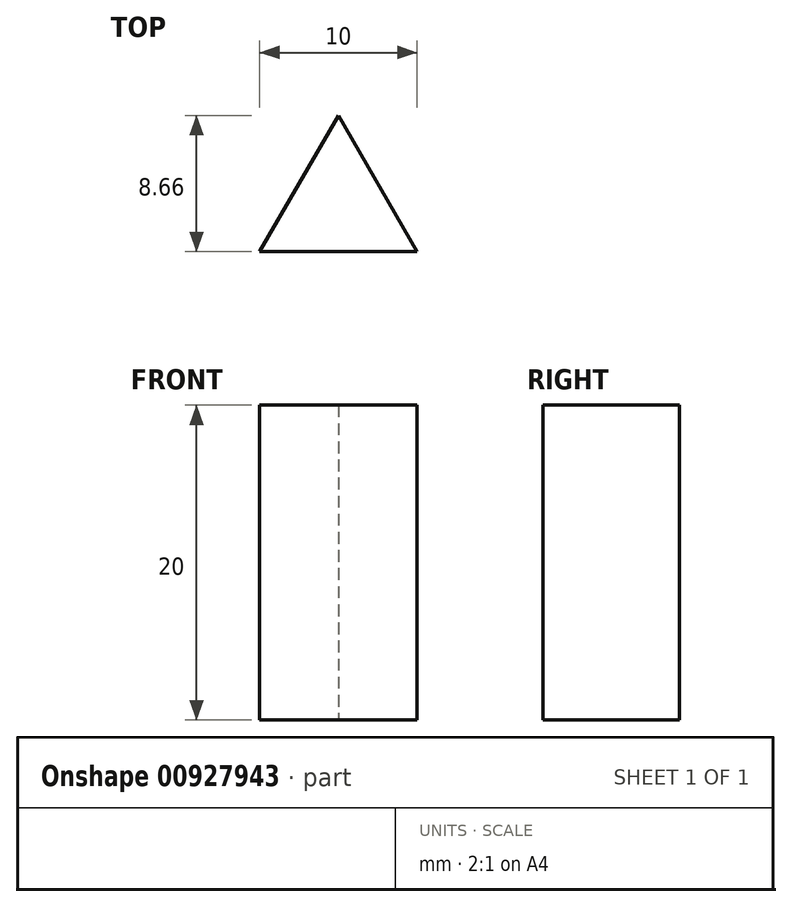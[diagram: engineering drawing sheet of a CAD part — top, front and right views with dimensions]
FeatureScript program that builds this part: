
annotation { "Feature Type Name" : "Feature", "Feature Type Description" : "" }
export const myFeature = defineFeature(function(context is Context, id is Id, definition is map)
    precondition{}
    {
        {
            var Q0;
            Q0=qCreatedBy(makeId("Top.planeOp"),FACE);
            var sketch = newSketch(context, id + "F0", { "sketchPlane" : qUnion([Q0])});
            skCircle(sketch, "E0.cCircle", {"center": v(0, 0) * mm, "radius": 2.89 * mm, "construction": true});
            skLineSegment(sketch, "E0.0", {"start": v(0, 5.77) * mm, "end": v(5, -2.89) * mm});
            skLineSegment(sketch, "E0.1", {"start": v(5, -2.89) * mm, "end": v(-5, -2.89) * mm});
            skLineSegment(sketch, "E0.2", {"start": v(-5, -2.89) * mm, "end": v(0, 5.77) * mm});
            skPoint(sketch, "E0.0.midPoint", {"position": v(2.5, 1.44) * mm});
            skSolve(sketch);
        }
        {
            var Q0;
            Q0 = qSketchRegion(id + "F0", true);
            extrude(context, id + "F1", {"entities" : qUnion([Q0]), "depth" : 20 * mm, "offsetDistance" : 25 * mm});
        }
    });
